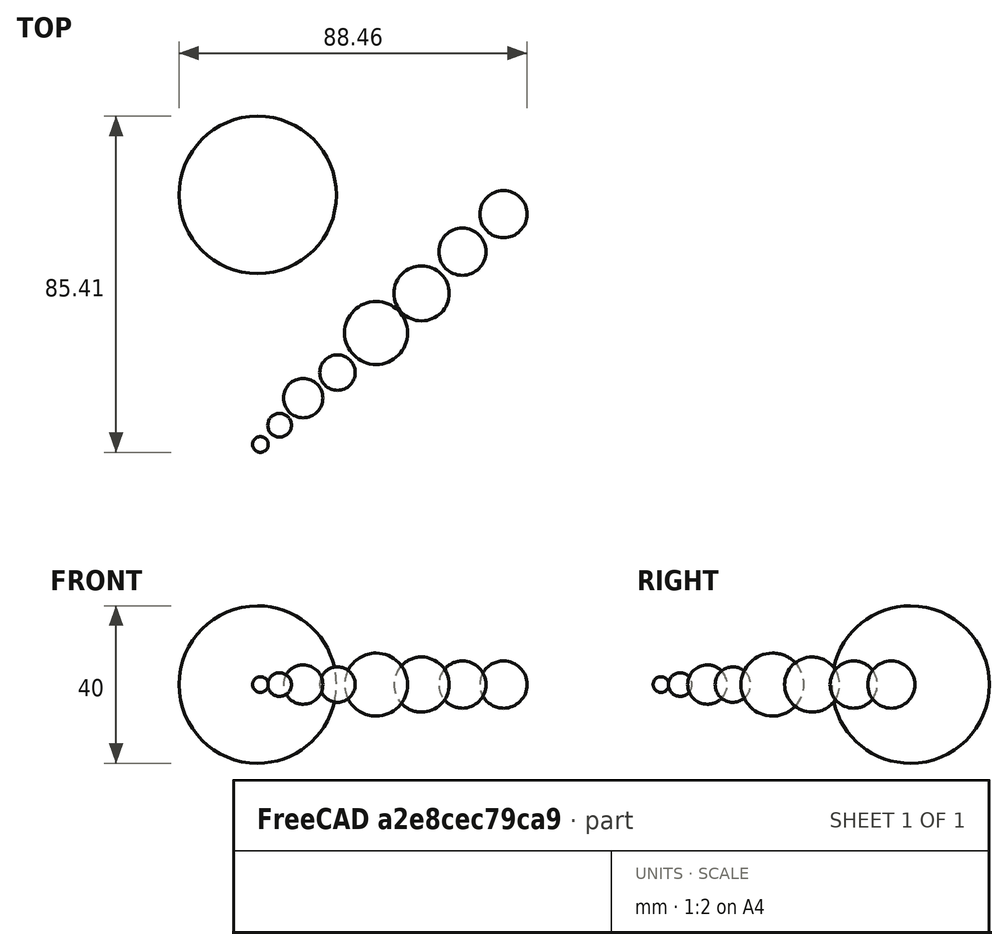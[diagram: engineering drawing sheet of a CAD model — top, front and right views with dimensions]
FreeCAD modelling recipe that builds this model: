
FCSTD DOCUMENT  (FreeCAD 0.19R24291 (Git))
Label: SystemeSolaire
License: All rights reserved
LicenseURL: http://en.wikipedia.org/wiki/All_rights_reserved
objects: Part::Sphere×9, Part::Ellipse×8
note: 17 computed .brp shape members not serialized (recipe doc carries the construction recipe); baked Part::Feature solids carry a one-line shape summary decoded from their .brp

FEATURE [Part::Sphere] Sphere  label="Mercure"
  Angle1 = -90
  Angle2 = 90
  Angle3 = 360
  AttacherType = Attacher::AttachEngine3D
  Placement = pos=(0.696497,-63.406,0) rot=(0,0,1;1.41372rad)
  Radius = 2
FEATURE [Part::Ellipse] Ellipse  label="OrbiteMercure"
  Angle0 = 0
  Angle1 = 360
  AttacherType = Attacher::AttachEngine3D
  MajorRadius = 50
  MinorRadius = 40
  Placement = pos=(0,0,0) rot=(0,-1,0;0.261799rad)
FEATURE [Part::Ellipse] Ellipse001  label="OrbiteVenus"
  Angle0 = 0
  Angle1 = 360
  AttacherType = Attacher::AttachEngine3D
  MajorRadius = 80
  MinorRadius = 70
  Placement = pos=(0,0,0) rot=(0,1,0;0.261799rad)
FEATURE [Part::Sphere] Sphere001  label="Venus"
  Angle1 = -90
  Angle2 = 90
  Angle3 = 360
  AttacherType = Attacher::AttachEngine3D
  Placement = pos=(5.57449,-58.5326,0) rot=(0,0,-1;1.65495rad)
  Radius = 3
FEATURE [Part::Ellipse] Ellipse002  label="OrbiteTerre"
  Angle0 = 0
  Angle1 = 360
  AttacherType = Attacher::AttachEngine3D
  MajorRadius = 120
  MinorRadius = 100
FEATURE [Part::Sphere] Sphere002  label="Terre"
  Angle1 = -90
  Angle2 = 90
  Angle3 = 360
  AttacherType = Attacher::AttachEngine3D
  Placement = pos=(11.5627,-51.6159,0) rot=(0,0,1;2.20348rad)
  Radius = 5
FEATURE [Part::Ellipse] Ellipse005  label="OrbiteMars"
  Angle0 = 0
  Angle1 = 360
  AttacherType = Attacher::AttachEngine3D
  MajorRadius = 140
  MinorRadius = 120
  Placement = pos=(0,0,0) rot=(0,-1,0;0.261799rad)
FEATURE [Part::Ellipse] Ellipse007  label="OrbiteJupiter"
  Angle0 = 0
  Angle1 = 360
  AttacherType = Attacher::AttachEngine3D
  MajorRadius = 200
  MinorRadius = 170
  Placement = pos=(0,0,0) rot=(0,1,0;0.261799rad)
FEATURE [Part::Ellipse] Ellipse008  label="OrbiteSaturne"
  Angle0 = 0
  Angle1 = 360
  AttacherType = Attacher::AttachEngine3D
  MajorRadius = 240
  MinorRadius = 210
  Placement = pos=(0,0,0) rot=(0,-1,0;0.261799rad)
FEATURE [Part::Ellipse] Ellipse009  label="OrbiteUranus"
  Angle0 = 0
  Angle1 = 360
  AttacherType = Attacher::AttachEngine3D
  MajorRadius = 280
  MinorRadius = 270
  Placement = pos=(0,0,0) rot=(0,1,0;0.261799rad)
FEATURE [Part::Ellipse] Ellipse010  label="OrbiteNeptune"
  Angle0 = 0
  Angle1 = 360
  AttacherType = Attacher::AttachEngine3D
  MajorRadius = 320
  MinorRadius = 300
  Placement = pos=(0,0,0) rot=(0,-1,0;0.261799rad)
FEATURE [Part::Sphere] Sphere004  label="Mars"
  Angle1 = -90
  Angle2 = 90
  Angle3 = 360
  AttacherType = Attacher::AttachEngine3D
  Placement = pos=(20.2803,-45.1481,0) rot=(0,0,1;0.01785rad)
  Radius = 4.5
FEATURE [Part::Sphere] Sphere005  label="Jupiter"
  Angle1 = -90
  Angle2 = 90
  Angle3 = 360
  AttacherType = Attacher::AttachEngine3D
  Placement = pos=(30.0906,-35.0689,0) rot=(0,0,1;2.96043rad)
  Radius = 8
FEATURE [Part::Sphere] Sphere006  label="Saturne"
  Angle1 = -90
  Angle2 = 90
  Angle3 = 360
  AttacherType = Attacher::AttachEngine3D
  Placement = pos=(41.6356,-25.0097,0) rot=(0,0,1;2.57872rad)
  Radius = 7
FEATURE [Part::Sphere] Sphere007  label="Uranus"
  Angle1 = -90
  Angle2 = 90
  Angle3 = 360
  AttacherType = Attacher::AttachEngine3D
  Placement = pos=(52.0193,-14.4279,0) rot=(0,0,-1;1.0626rad)
  Radius = 6
FEATURE [Part::Sphere] Sphere008  label="Neptune"
  Angle1 = -90
  Angle2 = 90
  Angle3 = 360
  AttacherType = Attacher::AttachEngine3D
  Placement = pos=(62.46,-4.87177,0) rot=(0,0,1;3.67896rad)
  Radius = 6
FEATURE [Part::Sphere] Sphere009  label="Soleil"
  Angle1 = -90
  Angle2 = 90
  Angle3 = 360
  AttacherType = Attacher::AttachEngine3D
  Placement = pos=(0,0,0) rot=(0,0,1;3.63247rad)
  Radius = 20
